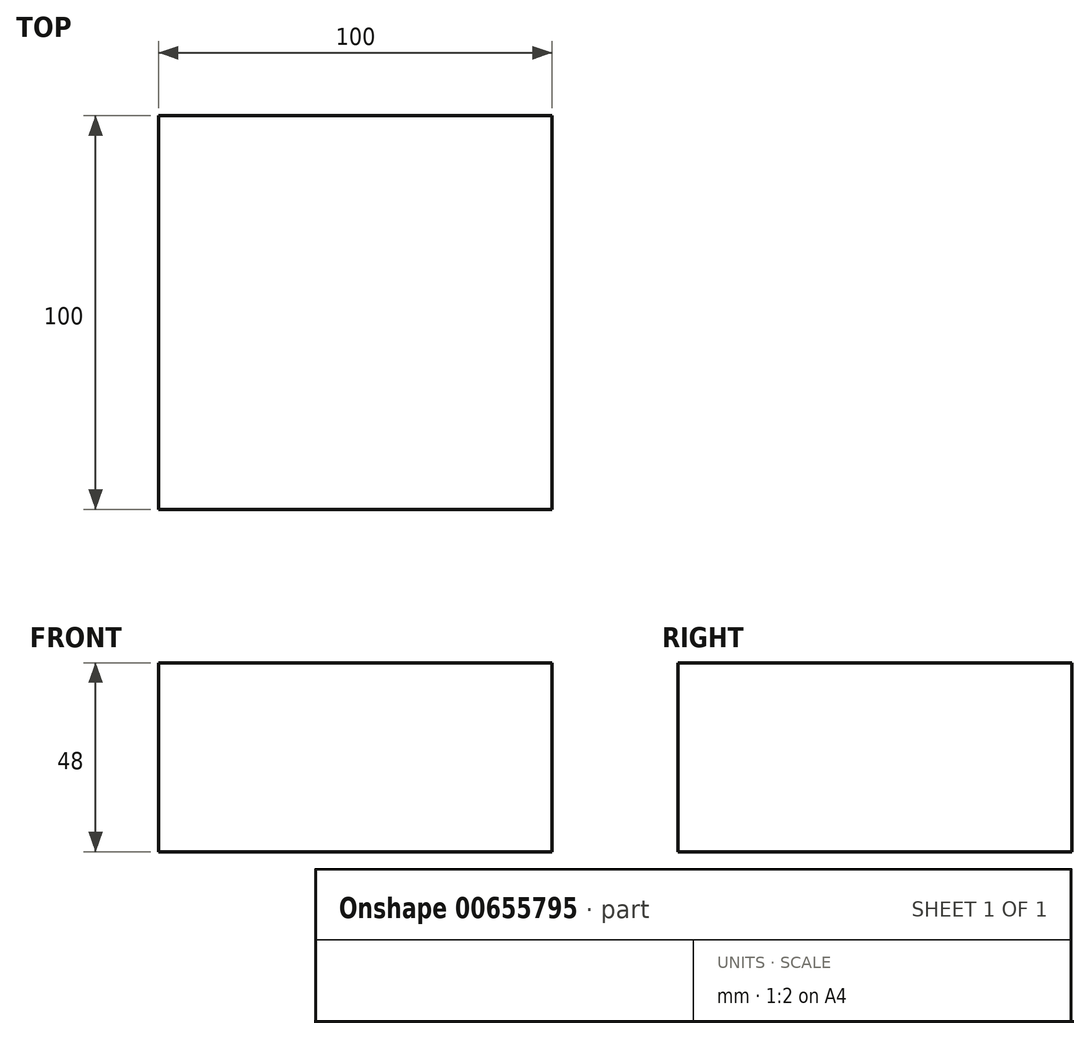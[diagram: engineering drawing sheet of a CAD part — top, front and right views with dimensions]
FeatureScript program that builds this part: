
annotation { "Feature Type Name" : "Feature", "Feature Type Description" : "" }
export const myFeature = defineFeature(function(context is Context, id is Id, definition is map)
    precondition{}
    {
        {
            var Q0;
            Q0=qCreatedBy(makeId("Top.planeOp"),FACE);
            var sketch = newSketch(context, id + "F0", { "sketchPlane" : qUnion([Q0])});
            skLineSegment(sketch, "E0.bottom", {"start": v(-42.65, 50.93) * mm, "end": v(57.35, 50.93) * mm});
            skLineSegment(sketch, "E0.top", {"start": v(-42.65, -49.07) * mm, "end": v(57.35, -49.07) * mm});
            skLineSegment(sketch, "E0.left", {"start": v(-42.65, 50.93) * mm, "end": v(-42.65, -49.07) * mm});
            skLineSegment(sketch, "E0.right", {"start": v(57.35, 50.93) * mm, "end": v(57.35, -49.07) * mm});
            skSolve(sketch);
        }
        {
            var Q0;
            Q0=makeQuery(id+"F0.imprint","IMPRINT",FACE,{"disambiguationData":[TD([[makeQuery(id+"F0.imprint","IMPRINT",EDGE,{"derivedFrom":sQuery(id+"F0.wireOp",EDGE,"E0.bottom")}),-1.0]])]});
            extrude(context, id + "F1", {"entities" : qUnion([Q0]), "depth" : 48 * mm, "offsetDistance" : 25 * mm});
        }
    });
